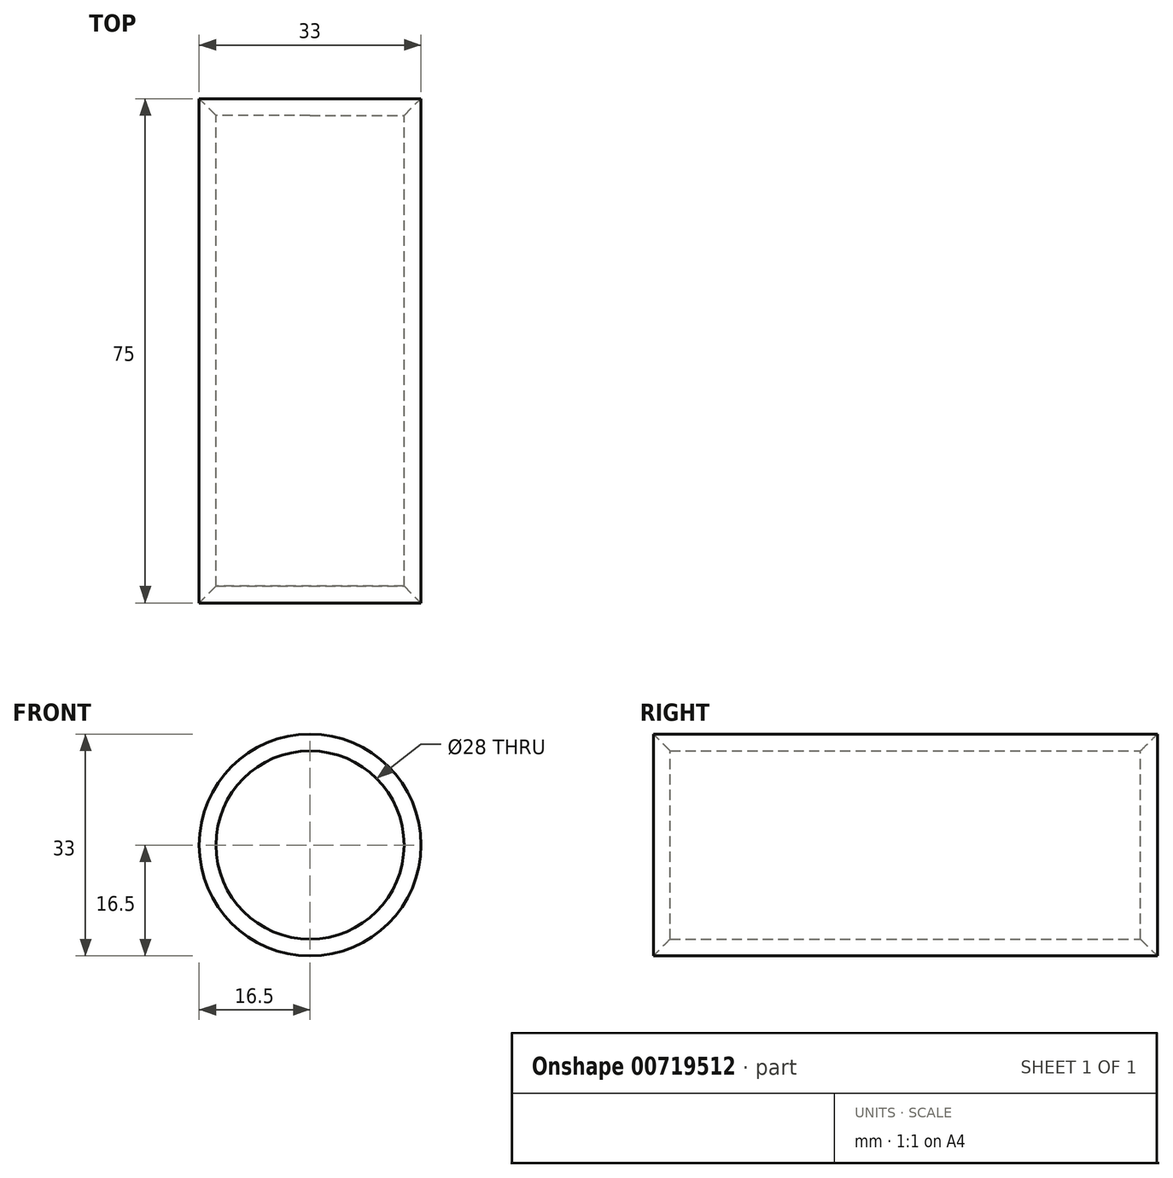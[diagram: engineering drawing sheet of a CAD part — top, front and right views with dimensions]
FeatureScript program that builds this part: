
annotation { "Feature Type Name" : "Feature", "Feature Type Description" : "" }
export const myFeature = defineFeature(function(context is Context, id is Id, definition is map)
    precondition{}
    {
        {
            var Q0;
            Q0=qCreatedBy(makeId("Front.planeOp"),FACE);
            var sketch = newSketch(context, id + "F0", { "sketchPlane" : qUnion([Q0])});
            skCircle(sketch, "E0", {"center": v(0, 0) * mm, "radius": 16.5 * mm});
            skCircle(sketch, "E1", {"center": v(0, 0) * mm, "radius": 14 * mm});
            skSolve(sketch);
        }
        {
            var Q0;
            Q0=makeQuery(id+"F0.imprint","IMPRINT",FACE,{"disambiguationData":[TD([[makeQuery(id+"F0.imprint","IMPRINT",EDGE,{"derivedFrom":sQuery(id+"F0.wireOp",EDGE,"E0")}),1.0]])]});
            extrude(context, id + "F1", {"entities" : qUnion([Q0]), "endBound" : BoundingType.SYMMETRIC, "depth" : 76 * mm, "offsetDistance" : 25 * mm});
        }
        {
            var Q0;
            Q0=makeQuery(id+"F1.opExtrude","CAP_EDGE",EDGE,{"disambiguationData":[OSD([sQuery(id+"F0.wireOp",EDGE,"E1")])],"isStart":false});
            var Q1;
            Q1=makeQuery(id+"F1.opExtrude","CAP_EDGE",EDGE,{"disambiguationData":[OSD([sQuery(id+"F0.wireOp",EDGE,"E1")])],"isStart":true});
            chamfer(context, id + "F2", {"entities" : qUnion([Q0, Q1]), "chamferType" : ChamferType.OFFSET_ANGLE, "width" : 3 * mm, "oppositeDirection" : false, "angle" : 45 * degree});
        }
    });
